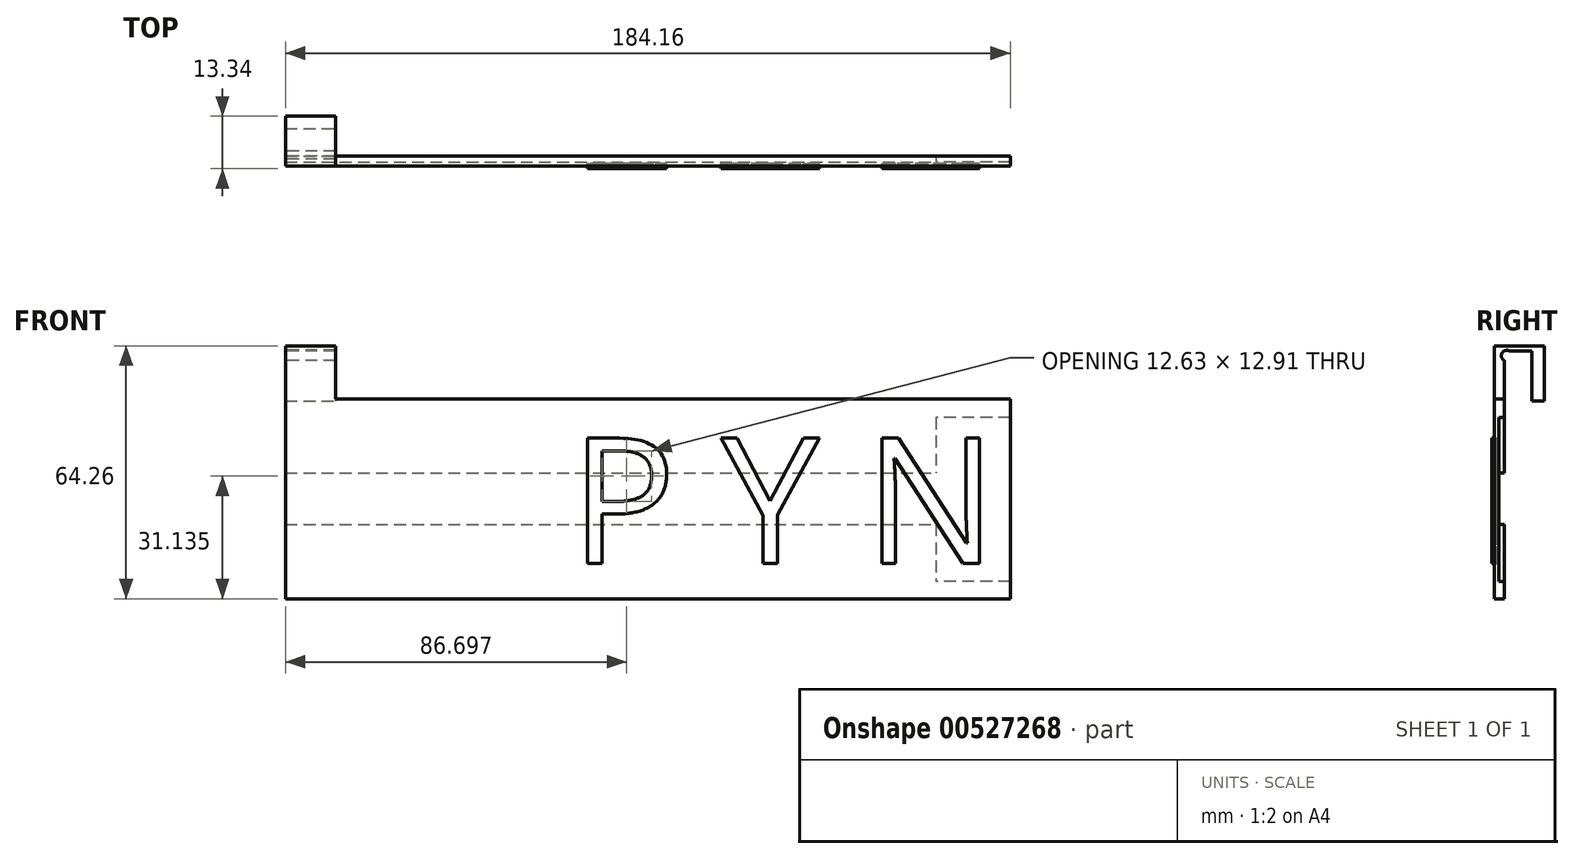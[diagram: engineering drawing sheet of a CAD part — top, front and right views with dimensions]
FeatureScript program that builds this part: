
annotation { "Feature Type Name" : "Feature", "Feature Type Description" : "" }
export const myFeature = defineFeature(function(context is Context, id is Id, definition is map)
    precondition{}
    {
        {
            var Q0;
            Q0=qCreatedBy(makeId("Front.planeOp"),FACE);
            var sketch = newSketch(context, id + "F0", { "sketchPlane" : qUnion([Q0])});
            skLineSegment(sketch, "E0.bottom", {"start": v(92.08, -25.4) * mm, "end": v(-92.08, -25.4) * mm});
            skLineSegment(sketch, "E0.top", {"start": v(92.08, 25.4) * mm, "end": v(-92.08, 25.4) * mm});
            skLineSegment(sketch, "E0.left", {"start": v(92.08, -25.4) * mm, "end": v(92.08, 25.4) * mm});
            skLineSegment(sketch, "E0.right", {"start": v(-92.08, -25.4) * mm, "end": v(-92.08, 25.4) * mm});
            skPoint(sketch, "E0.middle", {"position": v(0, 0) * mm});
            skSolve(sketch);
        }
        {
            var Q0;
            Q0=makeQuery(id+"F0.imprint","IMPRINT",FACE,{"disambiguationData":[TD([[makeQuery(id+"F0.imprint","IMPRINT",EDGE,{"derivedFrom":sQuery(id+"F0.wireOp",EDGE,"E0.bottom")}),-1.0]])]});
            var sketch = newSketch(context, id + "F1", { "sketchPlane" : qUnion([Q0])});
            skText(sketch, "E1", { "text": "P Y N", "fontName": "OpenSans-Regular.ttf"});
            const initialGuessF1  = {"E1": [-0.01976, -0.01639, 1, 0, 0.03205]};
            skSetInitialGuess(sketch, initialGuessF1);
            skSolve(sketch);
        }
        {
            var Q0;
            Q0 = qSketchRegion(id + "F1", true);
            extrude(context, id + "F2", {"entities" : qUnion([Q0]), "endBound" : BoundingType.SYMMETRIC, "depth" : 1.27 * mm, "offsetDistance" : 25.4 * mm});
        }
        {
            var Q0;
            Q0=makeQuery(id+"F0.imprint","IMPRINT",FACE,{"disambiguationData":[TD([[makeQuery(id+"F0.imprint","IMPRINT",EDGE,{"derivedFrom":sQuery(id+"F0.wireOp",EDGE,"E0.bottom")}),-1.0]])]});
            extrude(context, id + "F3", {"entities" : qUnion([Q0]), "oppositeDirection" : true, "depth" : 2.54 * mm, "offsetDistance" : 25.4 * mm});
        }
        {
            var Q0;
            Q0=makeQuery(id+"F3.opExtrude","CAP_FACE",FACE,{"disambiguationData":[OSD([sQuery(id+"F0.wireOp",EDGE,"E0.bottom"),sQuery(id+"F0.wireOp",EDGE,"E0.top"),sQuery(id+"F0.wireOp",EDGE,"E0.left"),sQuery(id+"F0.wireOp",EDGE,"E0.right")])],"isStart":false});
            var sketch = newSketch(context, id + "F4", { "sketchPlane" : qUnion([Q0])});
            skLineSegment(sketch, "E2.bottom", {"start": v(92.08, -6.5) * mm, "end": v(-92.08, -6.5) * mm});
            skLineSegment(sketch, "E2.top", {"start": v(92.08, 6.5) * mm, "end": v(-92.08, 6.5) * mm});
            skLineSegment(sketch, "E2.left", {"start": v(92.08, -6.5) * mm, "end": v(92.08, 6.5) * mm});
            skLineSegment(sketch, "E2.right", {"start": v(-92.08, -6.5) * mm, "end": v(-92.08, 6.5) * mm});
            skPoint(sketch, "E2.middle", {"position": v(0, 0) * mm});
            skSolve(sketch);
        }
        {
            var Q0;
            Q0=makeQuery(id+"F4.imprint","IMPRINT",FACE,{"disambiguationData":[TD([[makeQuery(id+"F4.imprint","IMPRINT",EDGE,{"derivedFrom":sQuery(id+"F4.wireOp",EDGE,"E2.bottom")}),-1.0]])]});
            extrude(context, id + "F5", {"entities" : qUnion([Q0]), "operationType" : NewBodyOperationType.REMOVE, "oppositeDirection" : true, "depth" : 1.45 * mm, "offsetDistance" : 25.4 * mm});
        }
        {
            var Q0;
            Q0=makeQuery(id+"F3.opExtrude","SWEPT_FACE",FACE,{"disambiguationData":[OSD([sQuery(id+"F0.wireOp",EDGE,"E0.top")])]});
            var sketch = newSketch(context, id + "F6", { "sketchPlane" : qUnion([Q0])});
            skLineSegment(sketch, "E3.bottom", {"start": v(-92.08, 0) * mm, "end": v(-79.38, 0) * mm});
            skLineSegment(sketch, "E3.top", {"start": v(-92.08, 2.54) * mm, "end": v(-79.38, 2.54) * mm});
            skLineSegment(sketch, "E3.left", {"start": v(-92.08, 0) * mm, "end": v(-92.08, 2.54) * mm});
            skLineSegment(sketch, "E3.right", {"start": v(-79.38, 0) * mm, "end": v(-79.38, 2.54) * mm});
            skSolve(sketch);
        }
        {
            var Q0;
            Q0=makeQuery(id+"F6.imprint","IMPRINT",FACE,{"disambiguationData":[TD([[makeQuery(id+"F6.imprint","IMPRINT",EDGE,{"derivedFrom":sQuery(id+"F6.wireOp",EDGE,"E3.bottom")}),-1.0]])]});
            extrude(context, id + "F7", {"entities" : qUnion([Q0]), "operationType" : NewBodyOperationType.ADD, "depth" : 13.46 * mm, "offsetDistance" : 25.4 * mm});
        }
        {
            var Q0;
            {var subQ0=sQuery(id+"F0.wireOp",EDGE,"E0.top");var subQ1=sQuery(id+"F0.wireOp",EDGE,"E0.left");var subQ2=sQuery(id+"F0.wireOp",EDGE,"E0.right");Q0=makeQuery(id+"F7.boolean.opBoolean","MERGE",FACE,{"derivedFrom":[makeQuery(id+"F5.boolean.opBoolean","SPLIT",FACE,{"disambiguationData":[TD([makeQuery(id+"F3.opExtrude","SWEPT_FACE",FACE,{"disambiguationData":[OSD([subQ0])]})])],"derivedFrom":makeQuery(id+"F3.opExtrude","CAP_FACE",FACE,{"disambiguationData":[OSD([sQuery(id+"F0.wireOp",EDGE,"E0.bottom"),subQ0,subQ1,subQ2])],"isStart":false})}),makeQuery(id+"F7.opExtrude","SWEPT_FACE",FACE,{"disambiguationData":[OSD([sQuery(id+"F6.wireOp",EDGE,"E3.top")])]})]});}
            var sketch = newSketch(context, id + "F8", { "sketchPlane" : qUnion([Q0])});
            skLineSegment(sketch, "E4.bottom", {"start": v(92.08, 38.86) * mm, "end": v(79.38, 38.86) * mm});
            skLineSegment(sketch, "E4.top", {"start": v(92.08, 37.6) * mm, "end": v(79.38, 37.6) * mm});
            skLineSegment(sketch, "E4.left", {"start": v(92.08, 38.86) * mm, "end": v(92.08, 37.6) * mm});
            skLineSegment(sketch, "E4.right", {"start": v(79.38, 38.86) * mm, "end": v(79.38, 37.6) * mm});
            skSolve(sketch);
        }
        {
            var Q0;
            Q0=makeQuery(id+"F8.imprint","IMPRINT",FACE,{"disambiguationData":[TD([[makeQuery(id+"F8.imprint","IMPRINT",EDGE,{"derivedFrom":sQuery(id+"F8.wireOp",EDGE,"E4.bottom")}),-1.0]])]});
            extrude(context, id + "F9", {"entities" : qUnion([Q0]), "operationType" : NewBodyOperationType.ADD, "depth" : 10.16 * mm, "offsetDistance" : 25.4 * mm});
        }
        {
            var Q0;
            Q0=makeQuery(id+"F9.opExtrude","SWEPT_FACE",FACE,{"disambiguationData":[OSD([sQuery(id+"F8.wireOp",EDGE,"E4.top")])]});
            var sketch = newSketch(context, id + "F10", { "sketchPlane" : qUnion([Q0])});
            skLineSegment(sketch, "E5.bottom", {"start": v(-92.08, -12.7) * mm, "end": v(-79.38, -12.7) * mm});
            skLineSegment(sketch, "E5.top", {"start": v(-92.08, -9.52) * mm, "end": v(-79.38, -9.52) * mm});
            skLineSegment(sketch, "E5.left", {"start": v(-92.08, -12.7) * mm, "end": v(-92.08, -9.52) * mm});
            skLineSegment(sketch, "E5.right", {"start": v(-79.38, -12.7) * mm, "end": v(-79.38, -9.52) * mm});
            skSolve(sketch);
        }
        {
            var Q0;
            Q0=makeQuery(id+"F10.imprint","IMPRINT",FACE,{"disambiguationData":[TD([[makeQuery(id+"F10.imprint","IMPRINT",EDGE,{"derivedFrom":sQuery(id+"F10.wireOp",EDGE,"E5.bottom")}),1.0]])]});
            extrude(context, id + "F11", {"entities" : qUnion([Q0]), "operationType" : NewBodyOperationType.ADD, "depth" : 12.7 * mm, "offsetDistance" : 25.4 * mm});
        }
        {
            var Q0;
            Q0=makeQuery(id+"F5.boolean.opBoolean","COPY",FACE,{"derivedFrom":makeQuery(id+"F5.opExtrude","CAP_FACE",FACE,{"disambiguationData":[OSD([sQuery(id+"F4.wireOp",EDGE,"E2.bottom"),sQuery(id+"F4.wireOp",EDGE,"E2.top"),sQuery(id+"F4.wireOp",EDGE,"E2.left"),sQuery(id+"F4.wireOp",EDGE,"E2.right")])],"isStart":false})});
            var sketch = newSketch(context, id + "F12", { "sketchPlane" : qUnion([Q0])});
            skLineSegment(sketch, "E6.bottom", {"start": v(-92.2, 20.62) * mm, "end": v(-73.14, 20.62) * mm});
            skLineSegment(sketch, "E6.top", {"start": v(-92.2, -21.03) * mm, "end": v(-73.14, -21.03) * mm});
            skLineSegment(sketch, "E6.left", {"start": v(-92.2, 20.62) * mm, "end": v(-92.2, -21.03) * mm});
            skLineSegment(sketch, "E6.right", {"start": v(-73.14, 20.62) * mm, "end": v(-73.14, -21.03) * mm});
            skSolve(sketch);
        }
        {
            var Q0;
            Q0 = qSketchRegion(id + "F12", true);
            extrude(context, id + "F13", {"entities" : qUnion([Q0]), "operationType" : NewBodyOperationType.REMOVE, "depth" : 13.2 * mm, "offsetDistance" : 25.4 * mm});
        }
        {
            var Q0;
            Q0=makeQuery(id+"F11.boolean.opBoolean","MERGE",FACE,{"derivedFrom":[makeQuery(id+"F9.boolean.opBoolean","MERGE",FACE,{"derivedFrom":[makeQuery(id+"F7.boolean.opBoolean","MERGE",FACE,{"derivedFrom":[makeQuery(id+"F3.opExtrude","SWEPT_FACE",FACE,{"disambiguationData":[OSD([sQuery(id+"F0.wireOp",EDGE,"E0.right")])]}),makeQuery(id+"F7.opExtrude","SWEPT_FACE",FACE,{"disambiguationData":[OSD([sQuery(id+"F6.wireOp",EDGE,"E3.left")])]})]}),makeQuery(id+"F9.opExtrude","SWEPT_FACE",FACE,{"disambiguationData":[OSD([sQuery(id+"F8.wireOp",EDGE,"E4.left")])]})]}),makeQuery(id+"F11.opExtrude","SWEPT_FACE",FACE,{"disambiguationData":[OSD([sQuery(id+"F10.wireOp",EDGE,"E5.left")])]})]});
            var sketch = newSketch(context, id + "F14", { "sketchPlane" : qUnion([Q0])});
            skCircle(sketch, "E7", {"center": v(-3.17, 36.35) * mm, "radius": 1.38 * mm});
            skSolve(sketch);
        }
        {
            var Q0;
            Q0 = qSketchRegion(id + "F14", true);
            extrude(context, id + "F15", {"entities" : qUnion([Q0]), "operationType" : NewBodyOperationType.REMOVE, "oppositeDirection" : true, "depth" : 25.4 * mm, "offsetDistance" : 25.4 * mm});
        }
    });
